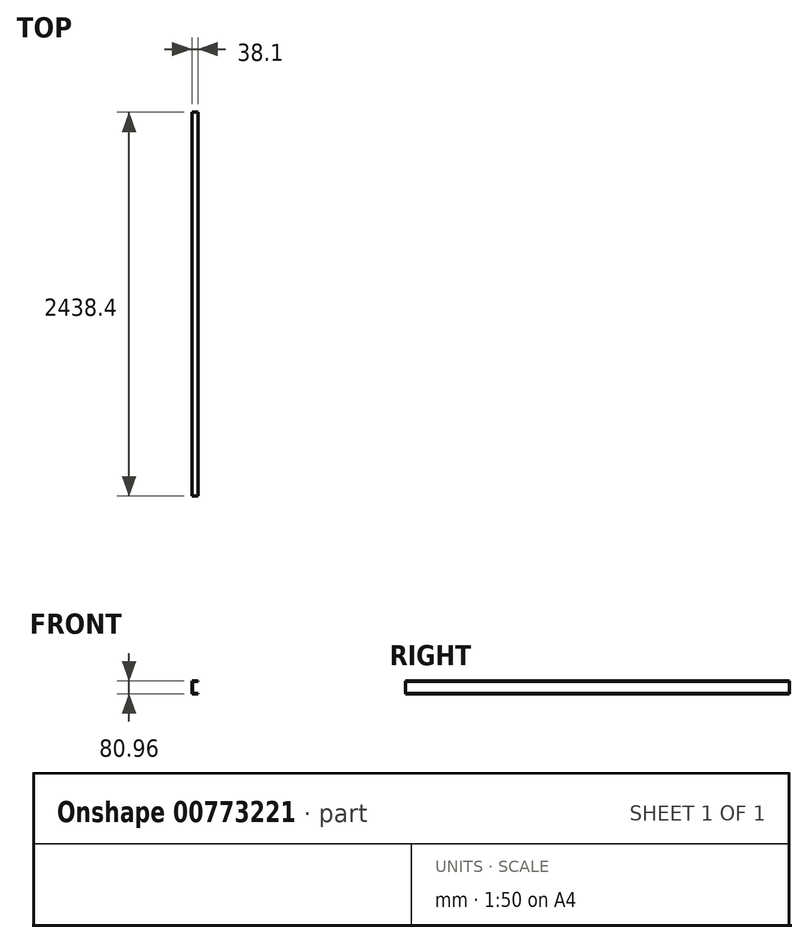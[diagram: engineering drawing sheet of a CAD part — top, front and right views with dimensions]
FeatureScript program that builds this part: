
annotation { "Feature Type Name" : "Feature", "Feature Type Description" : "" }
export const myFeature = defineFeature(function(context is Context, id is Id, definition is map)
    precondition{}
    {
        {
            var Q0;
            Q0=qCreatedBy(makeId("Front.planeOp"),FACE);
            var sketch = newSketch(context, id + "F0", { "sketchPlane" : qUnion([Q0])});
            skLineSegment(sketch, "E0", {"start": v(0, 0) * mm, "end": v(0, 80.96) * mm});
            skLineSegment(sketch, "E1", {"start": v(0, 80.96) * mm, "end": v(38.1, 80.96) * mm});
            skLineSegment(sketch, "E2", {"start": v(38.1, 80.96) * mm, "end": v(38.1, 77.79) * mm});
            skLineSegment(sketch, "E3", {"start": v(38.1, 77.79) * mm, "end": v(3.17, 77.79) * mm});
            skLineSegment(sketch, "E4", {"start": v(3.17, 77.79) * mm, "end": v(3.18, 3.17) * mm});
            skLineSegment(sketch, "E5", {"start": v(3.18, 3.17) * mm, "end": v(38.1, 3.18) * mm});
            skLineSegment(sketch, "E6", {"start": v(38.1, 3.18) * mm, "end": v(38.1, 0) * mm});
            skLineSegment(sketch, "E7", {"start": v(38.1, 0) * mm, "end": v(0, 0) * mm});
            skSolve(sketch);
        }
        {
            var Q0;
            Q0=qSketchRegion(id+"F0",true);
            extrude(context, id + "F1", {"entities" : qUnion([Q0]), "depth" : 2438.4 * mm, "offsetDistance" : 25.4 * mm});
        }
    });
